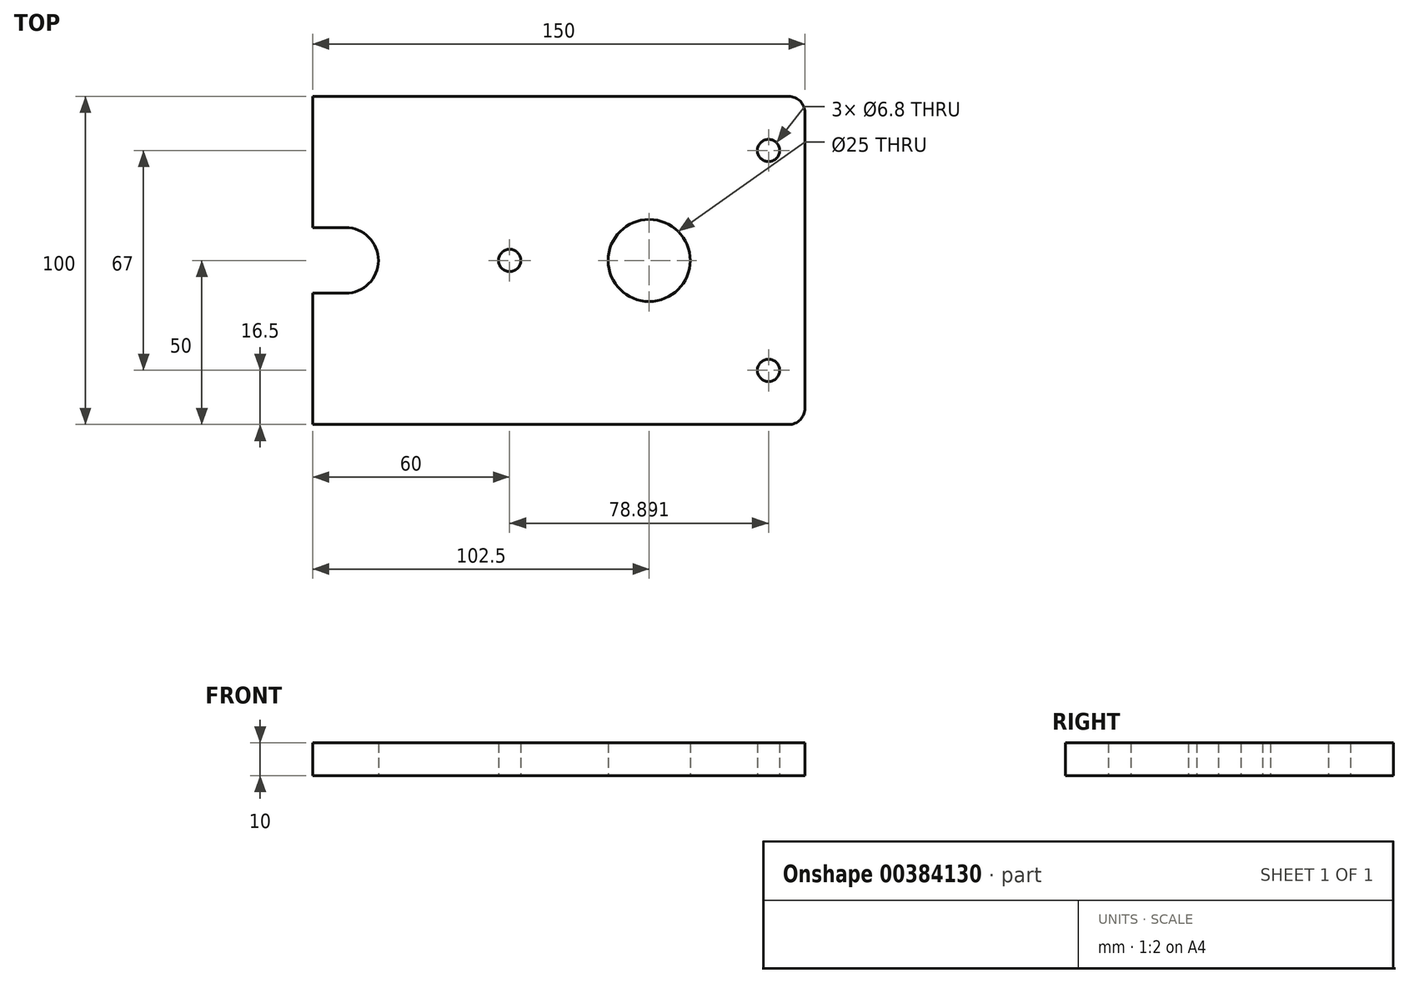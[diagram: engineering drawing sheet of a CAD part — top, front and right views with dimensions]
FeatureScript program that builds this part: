
annotation { "Feature Type Name" : "Feature", "Feature Type Description" : "" }
export const myFeature = defineFeature(function(context is Context, id is Id, definition is map)
    precondition{}
    {
        {
            var Q0;
            Q0=qCreatedBy(makeId("Top.planeOp"),FACE);
            var sketch = newSketch(context, id + "F0", { "sketchPlane" : qUnion([Q0])});
            skLineSegment(sketch, "E0.bottom", {"start": v(70, 50) * mm, "end": v(-75, 50) * mm});
            skLineSegment(sketch, "E0.top", {"start": v(70, -50) * mm, "end": v(-75, -50) * mm});
            skLineSegment(sketch, "E0.left", {"start": v(75, 45) * mm, "end": v(75, -45) * mm});
            skLineSegment(sketch, "E0.right", {"start": v(-75, 50) * mm, "end": v(-75, -50) * mm});
            skPoint(sketch, "E0.middle", {"position": v(0, 0) * mm});
            skCircle(sketch, "E1", {"center": v(63.9, 33.5) * mm, "radius": 3.4 * mm});
            skCircle(sketch, "E2", {"center": v(63.9, -33.5) * mm, "radius": 3.4 * mm});
            skCircle(sketch, "E3", {"center": v(27.5, 0) * mm, "radius": 12.5 * mm});
            skCircle(sketch, "E4", {"center": v(-15, 0) * mm, "radius": 3.4 * mm});
            skPoint(sketch, "E5.visualSharp", {"position": v(75, 50) * mm});
            skArc(sketch, "E5.filletArc", {"start": v(75, 45) * mm, "mid": v(73.54, 48.54) * mm, "end": v(70, 50) * mm});
            skPoint(sketch, "E6.visualSharp", {"position": v(75, -50) * mm});
            skArc(sketch, "E6.filletArc", {"start": v(70, -50) * mm, "mid": v(73.54, -48.54) * mm, "end": v(75, -45) * mm});
            skLineSegment(sketch, "E7.bottom", {"start": v(-65, -10) * mm, "end": v(-75, -10) * mm});
            skLineSegment(sketch, "E7.top", {"start": v(-65, 10) * mm, "end": v(-75, 10) * mm});
            skPoint(sketch, "E7.middle", {"position": v(-75, 0) * mm});
            skPoint(sketch, "E7.right.end.orphan", {"position": v(-85, 10) * mm});
            skPoint(sketch, "E8.orphan", {"position": v(-85, -10) * mm});
            skArc(sketch, "E9", {"start": v(-65, -10) * mm, "mid": v(-55, 0) * mm, "end": v(-65, 10) * mm});
            skSolve(sketch);
        }
        {
            var Q0;
            Q0=makeQuery(id+"F0.imprint","IMPRINT",FACE,{"disambiguationData":[TD([[makeQuery(id+"F0.imprint","IMPRINT",EDGE,{"derivedFrom":sQuery(id+"F0.wireOp",EDGE,"E0.bottom")}),1.0]])]});
            extrude(context, id + "F1", {"entities" : qUnion([Q0]), "depth" : 10 * mm});
        }
    });
